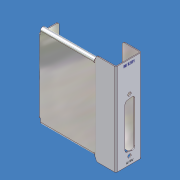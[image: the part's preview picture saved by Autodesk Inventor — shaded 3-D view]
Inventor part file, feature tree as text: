
AUTODESK INVENTOR PART (.ipt)
format: ipt  version: unknown  size: 564,224 bytes
history: native  units: mm (DEFAULTED — no unit token found)
features: sheet_metal_op x11, sketch x11, other x9, chamfer x3
ambient origin geometry x8: Origin, YZ Plane, XZ Plane, XY Plane, X Axis, Y Axis, Z Axis, Center Point
feature tree (34):
  sheet_metal_op  "Face1"
  sheet_metal_op  "Flange1"
  sheet_metal_op  "Flange2"
  chamfer  "Corner Round1"
  sheet_metal_op  "Face2"
  sheet_metal_op  "Flange3"
  chamfer  "Corner Round2"
  sheet_metal_op  "Hem2"
  sheet_metal_op  "Hem3"
  chamfer  "Corner Round3"
  sketch  "Sketch1"  dims[d0=22.86mm]
  other  "Plate1"
  sketch  "Sketch2"  dims[d1=80.5688mm]
  other  "Plate2"
  sheet_metal_op  "Bend1"
  sketch  "Sketch3"  dims[d2=0.7874mm]
  other  "Plate3"
  sheet_metal_op  "Bend2"
  sketch  "Sketch4"  dims[d3=0.7874mm]
  other  "Plate4"
  sheet_metal_op  "Bend3"
  sketch  "Sketch5"  dims[d4=0.3937mm]
  other  "Plate5"
  sheet_metal_op  "Bend4"
  sketch  "Sketch8"  dims[d5=1.5748mm]
  sketch  "Sketch9"  dims[d6=0.7874mm]
  sketch  "Sketch10"  dims[d7=16.51mm d8=90.0deg d9=0.7874mm]
  sketch  "Sketch11"  dims[d10=0.7874mm]
  sketch  "Sketch12"  dims[d11=0.3937mm]
  sketch  "Sketch15"  dims[d12=1.5748mm d13=0.7874mm d14=17.526mm d15=90.0deg d16=0.7874mm d17=1.778mm d18=0.7874mm d19=0.7874mm d20=0.3937mm d21=1.5748mm d22=0.7874mm d23=73.66mm d24=50.8mm d25=5.08mm d26=5.08mm d27=0.7874mm d28=0.3937mm d29=1.5748mm d30=0.7874mm d31=17.78mm d32=90.0deg d33=0.7874mm d42=1.778mm d43=0.7874mm d44=0.0mm d45=0.7874mm d46=0.3937mm d47=1.5748mm d48=0.7874mm d49=3.1496mm d50=2.7432mm d51=1.3716mm d52=0.7874mm d53=0.3937mm d54=1.5748mm d55=0.7874mm d56=3.1496mm d57=2.7432mm d58=1.3716mm d59=12.7mm d60=20.32mm d62=5.588mm d63=0.7874mm d64=0.0mm d65=1.778mm d66=3.175mm d67=3.048mm d69=23.5204mm d76=30.48mm d78=0.508mm d81=-15.707963mm]
  other  "Image3"
  other  "Cut1"
  other  "Cut2"
  other  "iFeature14:1"
